# Revit family: Trägerklammer F9-M12
name_source: partatom
category: HLS-Bauteile
revit_build: Autodesk Revit 2017 (Build: 20190507_1515(x64)
units: mm (PartAtom-declared; Revit-internal decimal feet)

## family parameters
Arbeitsebenenbasiert = Ja
Beim Laden mit Abzugskörper schneiden = Nein
Bemaßung runder Anschluss = Durchmesser verwenden
Gemeinsam genutzt = Ja
Immer vertikal = Nein
Raumberechnungspunkt = Nein
Teiletyp = Normal

## types (1)
- Trägerklammer F9-M12
    Artikelnummer = 0579703
    Befestigung = mit Durchgangsloch
    EAN = 4250928414793
    Fabrikat = MEFA
    Firma = MEFA Befestigungs- und Montagesysteme GmbH
    Gewicht = 0.52 kg
    Gewicht pro Bauteil = 0.52 kg
    Gewinde = für M12
    Kurztext1 = Trägerklammer Guss F9
    Kurztext2 = Klemmbereich 26 - 60 mm Loch für M12
    Material = Temperguss
    Mengeneinheit = St
    Oberflaeche = galvanisch verzinkt
    Stärke = 17 mm
    Vorgabe-Ansicht = 1219 mm
    max Klemmdicke = 0 mm  [stored 0 ft]
    max. zul. Last = 2.80 kN
    min. Klemmdicke = 26 mm
    vpe = 1 St

note: [stored X ft] marks values corroborated as IEEE doubles in the binary element streams (Revit-internal decimal feet)
